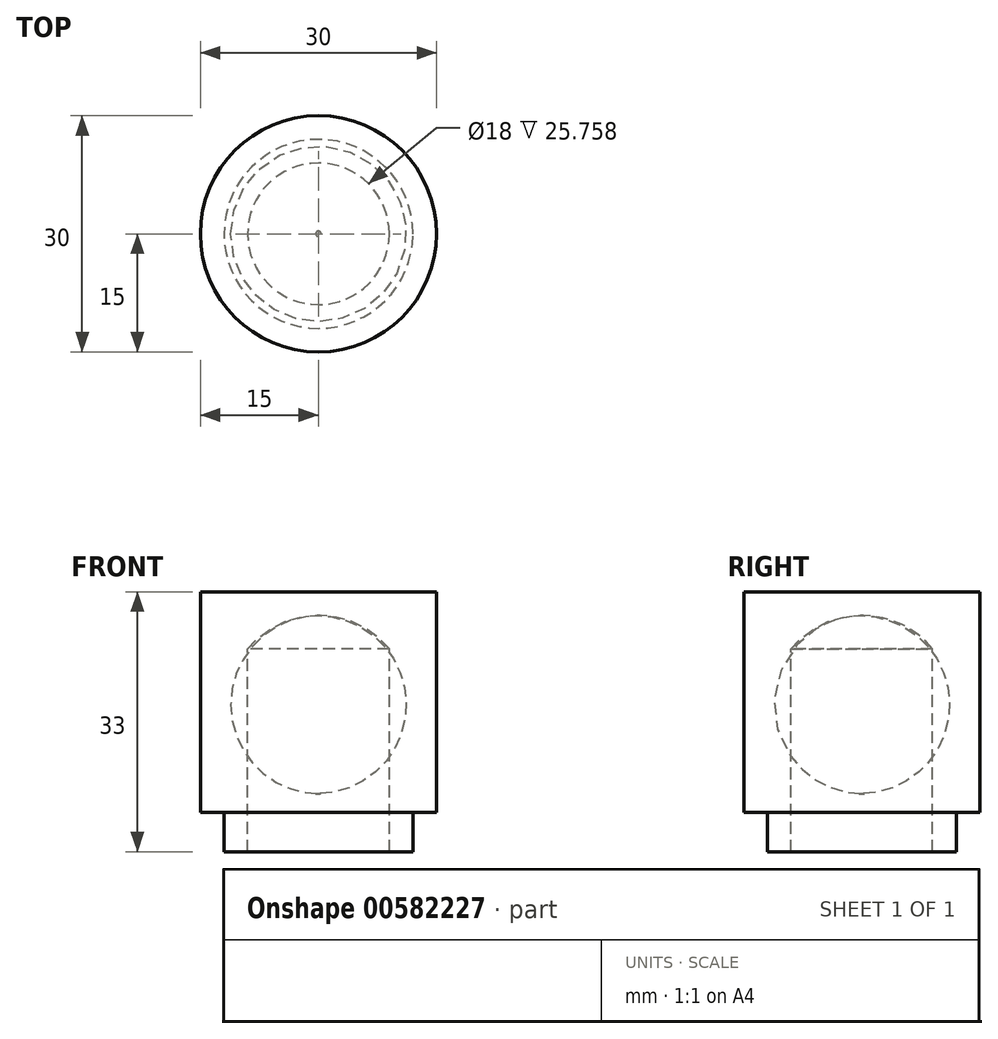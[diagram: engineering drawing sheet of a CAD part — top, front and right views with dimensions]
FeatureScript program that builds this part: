
annotation { "Feature Type Name" : "Feature", "Feature Type Description" : "" }
export const myFeature = defineFeature(function(context is Context, id is Id, definition is map)
    precondition{}
    {
        {
            var Q0;
            Q0=qCreatedBy(makeId("Front.planeOp"),FACE);
            var sketch = newSketch(context, id + "F0", { "sketchPlane" : qUnion([Q0])});
            skLineSegment(sketch, "E0.MirrorCS", {"start": v(-12, -28) * mm, "end": v(-15, -28) * mm});
            skLineSegment(sketch, "E1", {"start": v(-15, -6) * mm, "end": v(-15, 0) * mm});
            skLineSegment(sketch, "E2", {"start": v(-15, -6) * mm, "end": v(-15, -28) * mm});
            skLineSegment(sketch, "E3", {"start": v(-12, -28) * mm, "end": v(-12, -33) * mm});
            skLineSegment(sketch, "E4", {"start": v(-12, -33) * mm, "end": v(-9, -33) * mm});
            skLineSegment(sketch, "E5", {"start": v(-15, 0) * mm, "end": v(0, 0) * mm});
            skLineSegment(sketch, "E6.MirrorCS", {"start": v(15, 0) * mm, "end": v(0, 0) * mm});
            skLineSegment(sketch, "E7.MirrorCS", {"start": v(15, -3) * mm, "end": v(15, 0) * mm});
            skArc(sketch, "E8", {"start": v(9, -7.69) * mm, "mid": v(0.11, -3) * mm, "end": v(-9, -7.24) * mm});
            skLineSegment(sketch, "E9", {"start": v(-9, -33) * mm, "end": v(-9, -7.24) * mm});
            skLineSegment(sketch, "E10", {"start": v(0, 0) * mm, "end": v(0, -3) * mm});
            skLineSegment(sketch, "E11.MirrorCS", {"start": v(12, -33) * mm, "end": v(9, -33) * mm});
            skLineSegment(sketch, "E12.MirrorCS", {"start": v(12, -28) * mm, "end": v(12, -33) * mm});
            skLineSegment(sketch, "E13.MirrorCS", {"start": v(12, -28) * mm, "end": v(15, -28) * mm});
            skLineSegment(sketch, "E14", {"start": v(15, -28) * mm, "end": v(15, -3) * mm});
            skLineSegment(sketch, "E15", {"start": v(9, -33) * mm, "end": v(9, -7.69) * mm});
            skSolve(sketch);
        }
        {
            var Q0;
            {var subQ0=sQuery(id+"F0.wireOp",EDGE,"I7DhDJuf-7NLr-Svl4-PwQn-US4yEfDLbxPE.left");Q0=makeQuery(id+"F0.imprint","IMPRINT",FACE,{"disambiguationData":[TD([[makeQuery(id+"F0.imprint","IMPRINT",EDGE,{"derivedFrom":subQ0}),-1.0]])]});}
            var Q1;
            Q1=makeQuery(id+"F0.imprint","IMPRINT",FACE,{"disambiguationData":[TD([[makeQuery(id+"F0.imprint","IMPRINT",EDGE,{"derivedFrom":sQuery(id+"F0.wireOp",EDGE,"32eac864-653d-4b33-877a-62f6442f8a590.MirrorCS")}),1.0]])]});
            var Q2;
            Q2=makeQuery(id+"F0.imprint","IMPRINT",FACE,{"disambiguationData":[TD([[makeQuery(id+"F0.imprint","IMPRINT",EDGE,{"derivedFrom":sQuery(id+"F0.wireOp",EDGE,"E0.MirrorCS")}),-1.0]])]});
            var Q3;
            Q3=sQuery(id+"F0.wireOp",EDGE,"E10");
            revolve(context, id + "F1", {"entities" : qUnion([Q0, Q1, Q2]), "axis" : qUnion([Q3]), "revolveType" : RevolveType.FULL});
        }
    });
